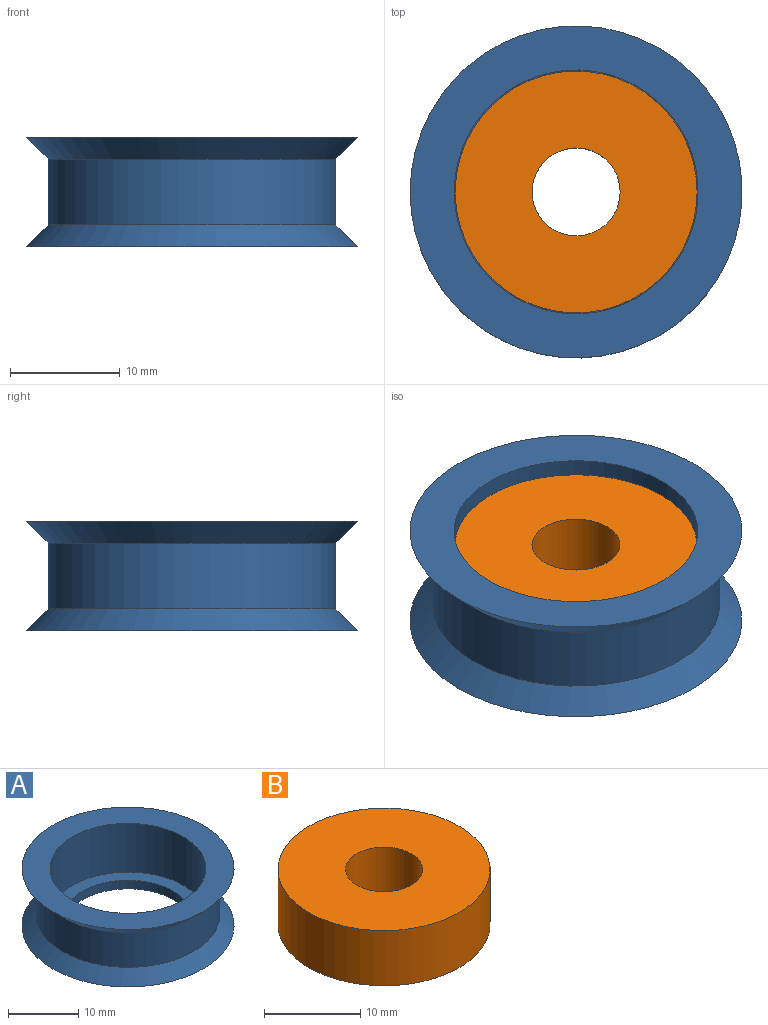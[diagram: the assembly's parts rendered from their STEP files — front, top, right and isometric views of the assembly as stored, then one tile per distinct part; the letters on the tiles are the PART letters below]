
ASSEMBLY  parts=2 mates=1
PART A: 8 faces, bbox 30.2x30.2x10 mm
  f0: plane 30.2x30.2mm, normal (0,0,1), area 329.2mm2, adj f1,f7
  f1: cylinder r=11.1mm len=22.2mm, axis (0,0,-1), area 592.8mm2, adj f0,f2
  f2: plane 22.2x22.2mm, normal (0,0,1), area 126.9mm2, adj f1,f3
  f3: cylinder r=9.1mm len=18.2mm, axis (0,0,-1), area 85.8mm2, adj f2,f4
  f4: plane 30.2x30.2mm, normal (0,0,-1), area 456.2mm2, adj f3,f5
  f5: cone r=13.1mm half-angle=45deg, axis (0,0,-1), area 250.6mm2, adj f4,f6
  f6: cylinder r=13.1mm len=26.2mm, axis (0,0,-1), area 493.9mm2, adj f5,f7
  f7: cone r=15.1mm half-angle=45deg, axis (0,0,1), area 250.6mm2, adj f0,f6
PART B: 4 faces, bbox 22x22x7 mm
  f0: cylinder r=4mm len=8mm, axis (0,0,-1), area 175.9mm2, adj f2,f3
  f1: cylinder r=11mm len=22mm, axis (0,0,-1), area 483.8mm2, adj f2,f3
  f2: plane 22x22mm, normal (0,0,1), area 329.9mm2, adj f0,f1
  f3: plane 22x22mm, normal (0,0,-1), area 329.9mm2, adj f0,f1
PLACE A t=(4.74,5.32,1.07)mm
PLACE B rot(axis=(1,0,0),180deg) t=(4.74,5.32,4.38)mm
MATE fastened B.f0 <-> A.f1  axis (0,0,1) through (4.74,5.32,-2.62)mm
